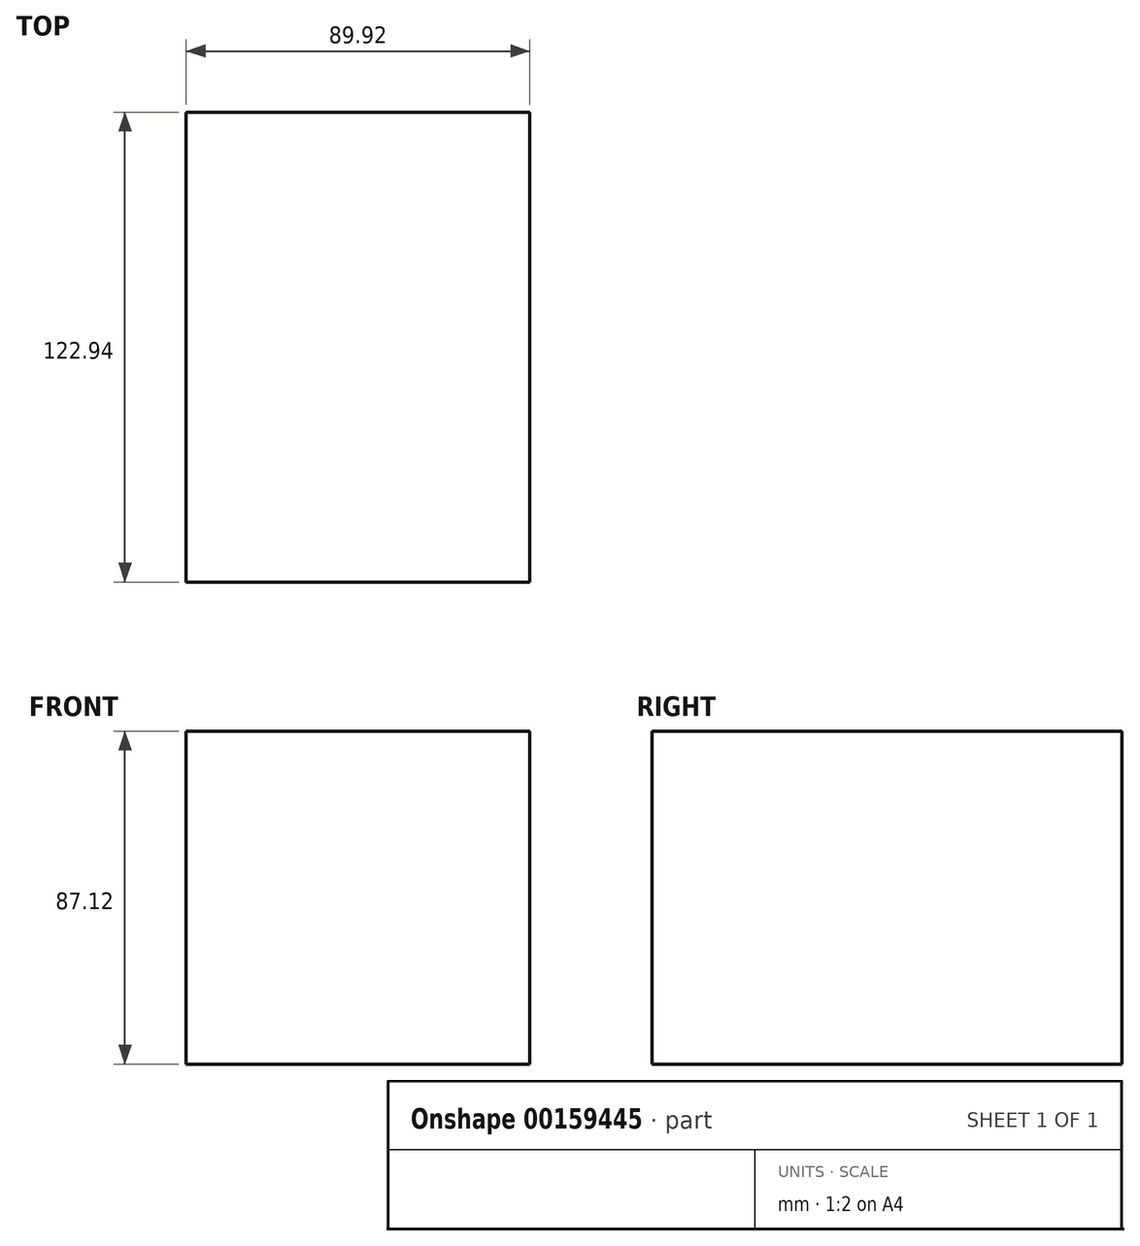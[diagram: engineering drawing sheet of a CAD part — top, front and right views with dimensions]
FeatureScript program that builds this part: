
annotation { "Feature Type Name" : "Feature", "Feature Type Description" : "" }
export const myFeature = defineFeature(function(context is Context, id is Id, definition is map)
    precondition{}
    {
        {
            var Q0;
            Q0=qCreatedBy(makeId("Front.planeOp"),FACE);
            var sketch = newSketch(context, id + "F0", { "sketchPlane" : qUnion([Q0])});
            skLineSegment(sketch, "E0.bottom", {"start": v(-44.96, 43.56) * mm, "end": v(44.96, 43.56) * mm});
            skLineSegment(sketch, "E0.top", {"start": v(-44.96, -43.56) * mm, "end": v(44.96, -43.56) * mm});
            skLineSegment(sketch, "E0.left", {"start": v(-44.96, 43.56) * mm, "end": v(-44.96, -43.56) * mm});
            skLineSegment(sketch, "E0.right", {"start": v(44.96, 43.56) * mm, "end": v(44.96, -43.56) * mm});
            skPoint(sketch, "E0.middle", {"position": v(0, 0) * mm});
            skSolve(sketch);
        }
        {
            var Q0;
            Q0=makeQuery(id+"F0.imprint","IMPRINT",FACE,{"disambiguationData":[TD([[makeQuery(id+"F0.imprint","IMPRINT",EDGE,{"derivedFrom":sQuery(id+"F0.wireOp",EDGE,"E0.bottom")}),-1.0]])]});
            extrude(context, id + "F1", {"entities" : qUnion([Q0]), "depth" : 122.94 * mm});
        }
    });
